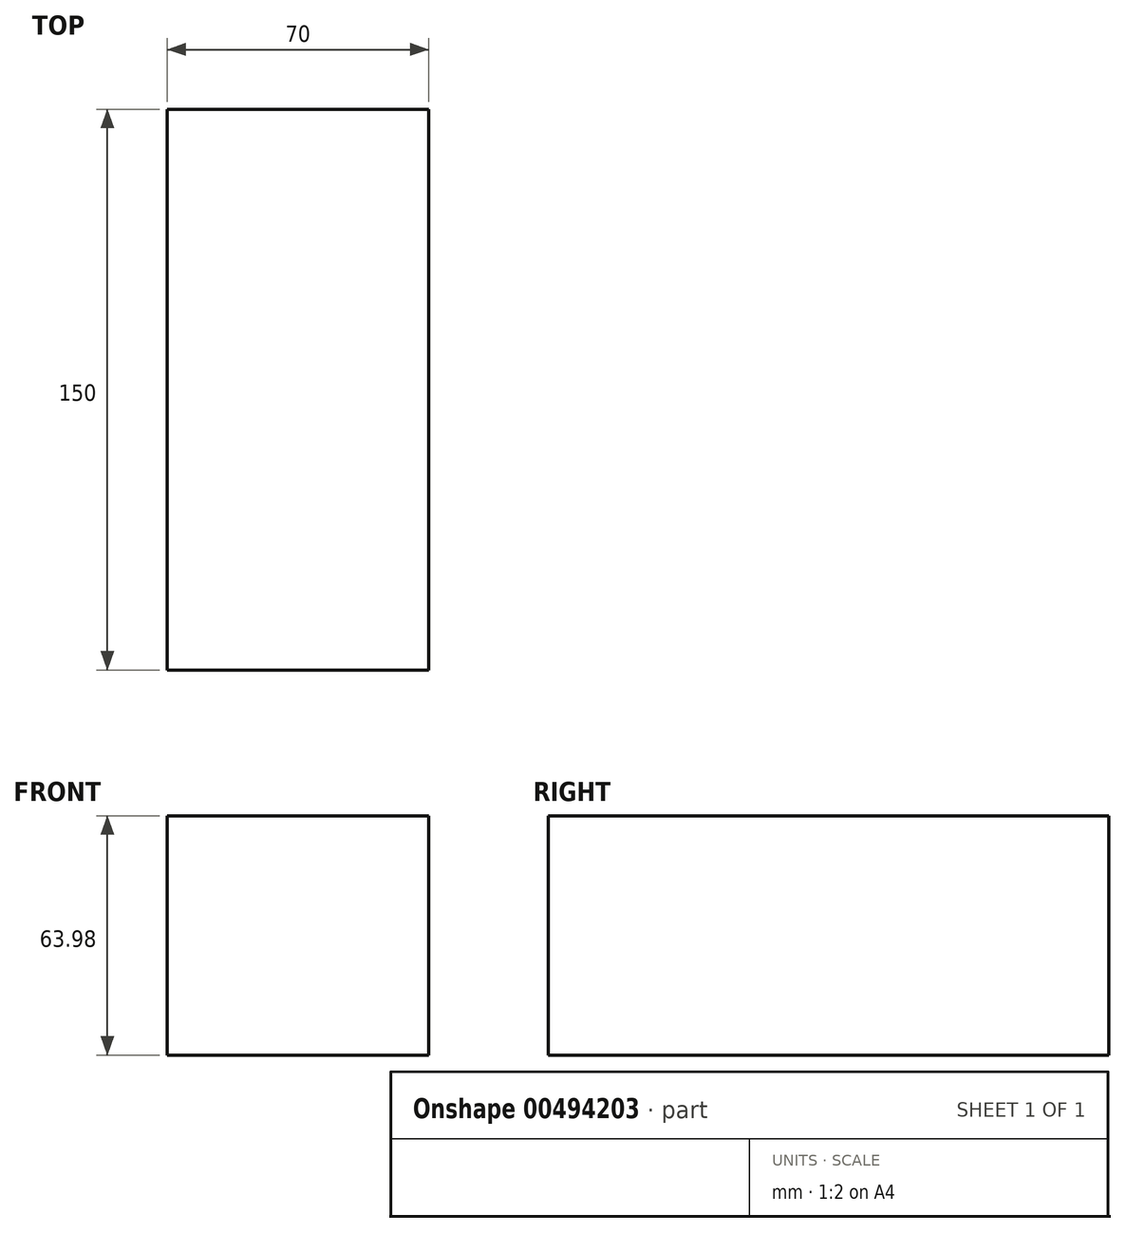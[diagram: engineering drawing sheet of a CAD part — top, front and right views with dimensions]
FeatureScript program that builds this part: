
annotation { "Feature Type Name" : "Feature", "Feature Type Description" : "" }
export const myFeature = defineFeature(function(context is Context, id is Id, definition is map)
    precondition{}
    {
        {
            var Q0;
            Q0=qCreatedBy(makeId("Front.planeOp"),FACE);
            var sketch = newSketch(context, id + "F0", { "sketchPlane" : qUnion([Q0])});
            skLineSegment(sketch, "E0.bottom", {"start": v(35, 31.99) * mm, "end": v(-35, 31.99) * mm});
            skLineSegment(sketch, "E0.top", {"start": v(35, -31.99) * mm, "end": v(-35, -31.99) * mm});
            skLineSegment(sketch, "E0.left", {"start": v(35, 31.99) * mm, "end": v(35, -31.99) * mm});
            skLineSegment(sketch, "E0.right", {"start": v(-35, 31.99) * mm, "end": v(-35, -31.99) * mm});
            skPoint(sketch, "E0.middle", {"position": v(0, 0) * mm});
            skSolve(sketch);
        }
        {
            var Q0;
            Q0=makeQuery(id+"F0.imprint","IMPRINT",FACE,{"disambiguationData":[TD([[makeQuery(id+"F0.imprint","IMPRINT",EDGE,{"derivedFrom":sQuery(id+"F0.wireOp",EDGE,"E0.bottom")}),1.0]])]});
            extrude(context, id + "F1", {"entities" : qUnion([Q0]), "depth" : 150 * mm});
        }
    });
